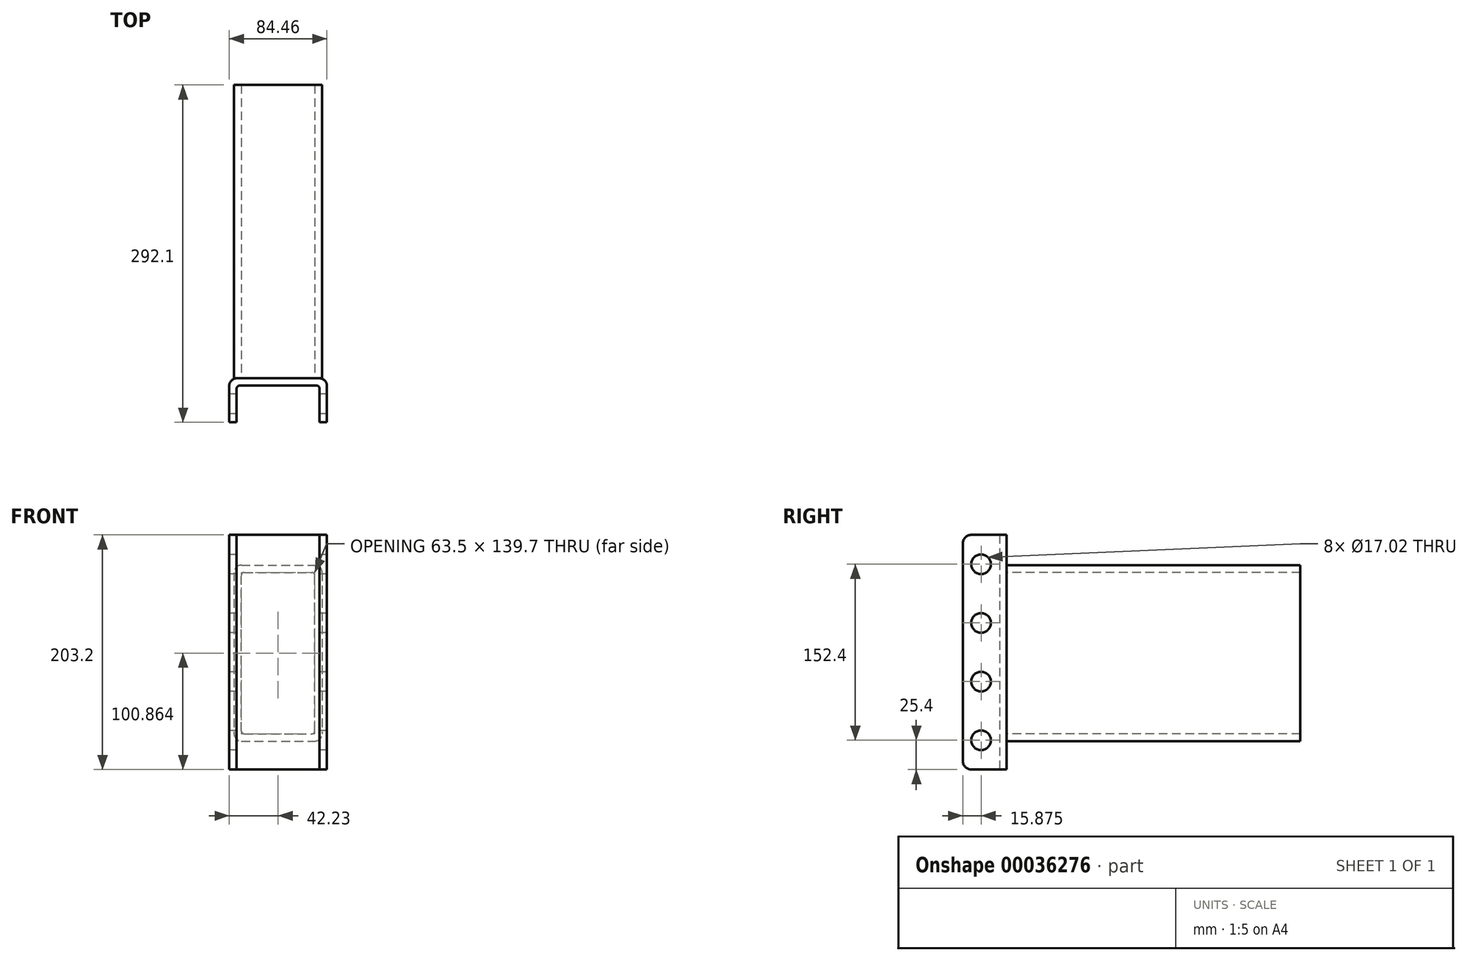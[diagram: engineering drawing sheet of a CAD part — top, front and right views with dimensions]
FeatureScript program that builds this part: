
annotation { "Feature Type Name" : "Feature", "Feature Type Description" : "" }
export const myFeature = defineFeature(function(context is Context, id is Id, definition is map)
    precondition{}
    {
        {
            var Q0;
            Q0=qCreatedBy(makeId("Top.planeOp"),FACE);
            var sketch = newSketch(context, id + "F0", { "sketchPlane" : qUnion([Q0])});
            skLineSegment(sketch, "E0", {"start": v(0, 0) * mm, "end": v(-35.88, 0) * mm});
            skLineSegment(sketch, "E1", {"start": v(-35.88, 0) * mm, "end": v(-35.88, -31.75) * mm});
            skLineSegment(sketch, "E2", {"start": v(0, 0) * mm, "end": v(0, -17.06) * mm, "construction": true});
            skLineSegment(sketch, "E3.MirrorCS", {"start": v(0, 0) * mm, "end": v(35.88, 0) * mm});
            skLineSegment(sketch, "E4.MirrorCS", {"start": v(35.88, 0) * mm, "end": v(35.88, -31.75) * mm});
            skLineSegment(sketch, "E5", {"start": v(-35.88, -31.75) * mm, "end": v(-42.23, -31.75) * mm});
            skLineSegment(sketch, "E6", {"start": v(-42.23, -31.75) * mm, "end": v(-42.23, 6.35) * mm});
            skLineSegment(sketch, "E7", {"start": v(-42.23, 6.35) * mm, "end": v(0, 6.35) * mm});
            skLineSegment(sketch, "E8.MirrorCS", {"start": v(42.23, 6.35) * mm, "end": v(0, 6.35) * mm});
            skLineSegment(sketch, "E9.MirrorCS", {"start": v(42.23, -31.75) * mm, "end": v(42.23, 6.35) * mm});
            skLineSegment(sketch, "E10.MirrorCS", {"start": v(35.88, -31.75) * mm, "end": v(42.23, -31.75) * mm});
            skLineSegment(sketch, "E11", {"start": v(0, 0) * mm, "end": v(0, 6.35) * mm, "construction": true});
            skSolve(sketch);
        }
        {
            var Q0;
            Q0=makeQuery(id+"F0.imprint","IMPRINT",FACE,{"disambiguationData":[TD([[makeQuery(id+"F0.imprint","IMPRINT",EDGE,{"derivedFrom":sQuery(id+"F0.wireOp",EDGE,"E0")}),-1.0]])]});
            extrude(context, id + "F1", {"entities" : qUnion([Q0]), "depth" : 203.2 * mm});
        }
        {
            var Q0;
            Q0=makeQuery(id+"F1.opExtrude","SWEPT_EDGE",EDGE,{"disambiguationData":[OSD([sQuery(id+"F0.wireOp",EDGE,"E8.MirrorCS"),sQuery(id+"F0.wireOp",EDGE,"E9.MirrorCS")])]});
            var Q1;
            Q1=makeQuery(id+"F1.opExtrude","SWEPT_EDGE",EDGE,{"disambiguationData":[OSD([sQuery(id+"F0.wireOp",EDGE,"E6"),sQuery(id+"F0.wireOp",EDGE,"E7")])]});
            fillet(context, id + "F2", {"entities" : qUnion([Q0, Q1]), "radius" : 6.35 * mm, "tangentPropagation" : true, "allowEdgeOverflow" : false});
        }
        {
            var Q0;
            Q0=makeQuery(id+"F1.opExtrude","CAP_EDGE",EDGE,{"disambiguationData":[OSD([sQuery(id+"F0.wireOp",EDGE,"E5")])],"isStart":false});
            var Q1;
            Q1=makeQuery(id+"F1.opExtrude","CAP_EDGE",EDGE,{"disambiguationData":[OSD([sQuery(id+"F0.wireOp",EDGE,"E10.MirrorCS")])],"isStart":false});
            var Q2;
            Q2=makeQuery(id+"F1.opExtrude","CAP_EDGE",EDGE,{"disambiguationData":[OSD([sQuery(id+"F0.wireOp",EDGE,"E5")])],"isStart":true});
            var Q3;
            Q3=makeQuery(id+"F1.opExtrude","CAP_EDGE",EDGE,{"disambiguationData":[OSD([sQuery(id+"F0.wireOp",EDGE,"E10.MirrorCS")])],"isStart":true});
            fillet(context, id + "F3", {"entities" : qUnion([Q0, Q1, Q2, Q3]), "radius" : 7.62 * mm, "tangentPropagation" : true, "allowEdgeOverflow" : false});
        }
        {
            var Q0;
            Q0=makeQuery(id+"F1.opExtrude","SWEPT_FACE",FACE,{"disambiguationData":[OSD([sQuery(id+"F0.wireOp",EDGE,"E6")])]});
            var sketch = newSketch(context, id + "F4", { "sketchPlane" : qUnion([Q0])});
            skCircle(sketch, "E12", {"center": v(15.88, 25.4) * mm, "radius": 8.5 * mm});
            skLineSegment(sketch, "E13", {"start": v(0, 101.6) * mm, "end": v(31.75, 101.6) * mm, "construction": true});
            skLineSegment(sketch, "E14", {"start": v(15.87, 203.2) * mm, "end": v(15.88, 0) * mm, "construction": true});
            skPoint(sketch, "E15", {"position": v(15.88, 101.6) * mm});
            skCircle(sketch, "E16.0.1.0", {"center": v(15.88, 76.2) * mm, "radius": 8.5 * mm});
            skCircle(sketch, "E16.0.2.0", {"center": v(15.88, 127) * mm, "radius": 8.5 * mm});
            skCircle(sketch, "E16.0.3.0", {"center": v(15.88, 177.8) * mm, "radius": 8.5 * mm});
            skLineSegment(sketch, "E16.direction1", {"start": v(15.88, 25.4) * mm, "end": v(40.64, 25.4) * mm, "construction": true});
            skLineSegment(sketch, "E16.direction2", {"start": v(15.88, 25.4) * mm, "end": v(15.88, 76.2) * mm, "construction": true});
            skLineSegment(sketch, "E17", {"start": v(15.87, 177.8) * mm, "end": v(15.87, 203.2) * mm, "construction": true});
            skLineSegment(sketch, "E18", {"start": v(15.88, 127) * mm, "end": v(15.88, 101.6) * mm, "construction": true});
            skLineSegment(sketch, "E19", {"start": v(15.88, 0) * mm, "end": v(15.88, 25.4) * mm, "construction": true});
            skSolve(sketch);
        }
        {
            var Q0;
            Q0=makeQuery(id+"F4.imprint","IMPRINT",FACE,{"disambiguationData":[TD([[makeQuery(id+"F4.imprint","IMPRINT",EDGE,{"derivedFrom":sQuery(id+"F4.wireOp",EDGE,"E16.0.3.0")}),1.0]])]});
            var Q1;
            Q1=makeQuery(id+"F4.imprint","IMPRINT",FACE,{"disambiguationData":[TD([[makeQuery(id+"F4.imprint","IMPRINT",EDGE,{"derivedFrom":sQuery(id+"F4.wireOp",EDGE,"E16.0.2.0")}),1.0]])]});
            var Q2;
            Q2=makeQuery(id+"F4.imprint","IMPRINT",FACE,{"disambiguationData":[TD([[makeQuery(id+"F4.imprint","IMPRINT",EDGE,{"derivedFrom":sQuery(id+"F4.wireOp",EDGE,"E16.0.1.0")}),1.0]])]});
            var Q3;
            Q3=makeQuery(id+"F4.imprint","IMPRINT",FACE,{"disambiguationData":[TD([[makeQuery(id+"F4.imprint","IMPRINT",EDGE,{"derivedFrom":sQuery(id+"F4.wireOp",EDGE,"E12")}),1.0]])]});
            extrude(context, id + "F5", {"entities" : qUnion([Q0, Q1, Q2, Q3]), "operationType" : NewBodyOperationType.REMOVE, "endBound" : BoundingType.THROUGH_ALL, "oppositeDirection" : true, "depth" : 25.4 * mm});
        }
        {
            var Q0;
            Q0=makeQuery(id+"F1.opExtrude","SWEPT_EDGE",EDGE,{"disambiguationData":[OSD([sQuery(id+"F0.wireOp",EDGE,"E3.MirrorCS"),sQuery(id+"F0.wireOp",EDGE,"E4.MirrorCS")])]});
            var Q1;
            Q1=makeQuery(id+"F1.opExtrude","SWEPT_EDGE",EDGE,{"disambiguationData":[OSD([sQuery(id+"F0.wireOp",EDGE,"E0"),sQuery(id+"F0.wireOp",EDGE,"E1")])]});
            fillet(context, id + "F6", {"entities" : qUnion([Q0, Q1]), "radius" : 2.54 * mm, "tangentPropagation" : true, "allowEdgeOverflow" : false});
        }
        {
            var Q0;
            Q0=makeQuery(id+"F1.opExtrude","SWEPT_FACE",FACE,{"disambiguationData":[OSD([sQuery(id+"F0.wireOp",EDGE,"E7"),sQuery(id+"F0.wireOp",EDGE,"E8.MirrorCS")])]});
            var sketch = newSketch(context, id + "F7", { "sketchPlane" : qUnion([Q0])});
            skLineSegment(sketch, "E20.rect.bottom", {"start": v(38.1, 177.06) * mm, "end": v(-38.1, 177.06) * mm});
            skLineSegment(sketch, "E20.rect.top", {"start": v(38.1, 24.66) * mm, "end": v(-38.1, 24.66) * mm});
            skLineSegment(sketch, "E20.rect.left", {"start": v(38.1, 177.06) * mm, "end": v(38.1, 24.66) * mm});
            skLineSegment(sketch, "E20.rect.right", {"start": v(-38.1, 177.06) * mm, "end": v(-38.1, 24.66) * mm});
            skPoint(sketch, "E20.rect.middle", {"position": v(0, 100.86) * mm});
            skLineSegment(sketch, "E21.rect.bottom", {"start": v(31.75, 31.01) * mm, "end": v(-31.75, 31.01) * mm});
            skLineSegment(sketch, "E21.rect.top", {"start": v(31.75, 170.71) * mm, "end": v(-31.75, 170.71) * mm});
            skLineSegment(sketch, "E21.rect.left", {"start": v(31.75, 31.01) * mm, "end": v(31.75, 170.71) * mm});
            skLineSegment(sketch, "E21.rect.right", {"start": v(-31.75, 31.01) * mm, "end": v(-31.75, 170.71) * mm});
            skSolve(sketch);
        }
        {
            var Q0;
            {var subQ6=sQuery(id+"F7.wireOp",EDGE,"E20.rect.left");Q0=makeQuery(id+"F7.imprint","IMPRINT",FACE,{"disambiguationData":[TD([[makeQuery(id+"F7.imprint","IMPRINT",EDGE,{"derivedFrom":subQ6}),-1.0]])]});}
            var Q1;
            Q1=makeQuery(id+"F7.imprint","IMPRINT",FACE,{"disambiguationData":[TD([[makeQuery(id+"F7.imprint","IMPRINT",EDGE,{"derivedFrom":sQuery(id+"F7.wireOp",EDGE,"E21.rect.bottom")}),1.0]])]});
            var Q2;
            {var subQ6=sQuery(id+"F7.wireOp",EDGE,"E20.rect.right");Q2=makeQuery(id+"F7.imprint","IMPRINT",FACE,{"disambiguationData":[TD([[makeQuery(id+"F7.imprint","IMPRINT",EDGE,{"derivedFrom":subQ6}),1.0]])]});}
            extrude(context, id + "F8", {"entities" : qUnion([Q0, Q1, Q2]), "depth" : 254 * mm});
        }
        {
            var Q0;
            Q0=makeQuery(id+"F8.opExtrude","SWEPT_EDGE",EDGE,{"disambiguationData":[OSD([sQuery(id+"F0.wireOp",EDGE,"E7"),sQuery(id+"F0.wireOp",EDGE,"E8.MirrorCS"),sQuery(id+"F0.wireOp",EDGE,"E9.MirrorCS"),sQuery(id+"F7.wireOp",EDGE,"E20.rect.bottom")])]});
            var Q1;
            Q1=makeQuery(id+"F8.opExtrude","SWEPT_EDGE",EDGE,{"disambiguationData":[OSD([sQuery(id+"F0.wireOp",EDGE,"E6"),sQuery(id+"F0.wireOp",EDGE,"E7"),sQuery(id+"F0.wireOp",EDGE,"E8.MirrorCS"),sQuery(id+"F7.wireOp",EDGE,"E20.rect.bottom")])]});
            var Q2;
            Q2=makeQuery(id+"F8.opExtrude","SWEPT_EDGE",EDGE,{"disambiguationData":[OSD([sQuery(id+"F0.wireOp",EDGE,"E7"),sQuery(id+"F0.wireOp",EDGE,"E8.MirrorCS"),sQuery(id+"F0.wireOp",EDGE,"E9.MirrorCS"),sQuery(id+"F7.wireOp",EDGE,"E20.rect.top")])]});
            var Q3;
            Q3=makeQuery(id+"F8.opExtrude","SWEPT_EDGE",EDGE,{"disambiguationData":[OSD([sQuery(id+"F0.wireOp",EDGE,"E6"),sQuery(id+"F0.wireOp",EDGE,"E7"),sQuery(id+"F0.wireOp",EDGE,"E8.MirrorCS"),sQuery(id+"F7.wireOp",EDGE,"E20.rect.top")])]});
            fillet(context, id + "F9", {"entities" : qUnion([Q0, Q1, Q2, Q3]), "radius" : 6.35 * mm, "tangentPropagation" : true, "allowEdgeOverflow" : false});
        }
        {
            var Q0;
            Q0=makeQuery(id+"F8.opExtrude","SWEPT_EDGE",EDGE,{"disambiguationData":[OSD([sQuery(id+"F7.wireOp",EDGE,"E21.rect.top"),sQuery(id+"F7.wireOp",EDGE,"E21.rect.right")])]});
            var Q1;
            Q1=makeQuery(id+"F8.opExtrude","SWEPT_EDGE",EDGE,{"disambiguationData":[OSD([sQuery(id+"F7.wireOp",EDGE,"E21.rect.top"),sQuery(id+"F7.wireOp",EDGE,"E21.rect.left")])]});
            var Q2;
            Q2=makeQuery(id+"F8.opExtrude","SWEPT_EDGE",EDGE,{"disambiguationData":[OSD([sQuery(id+"F7.wireOp",EDGE,"E21.rect.bottom"),sQuery(id+"F7.wireOp",EDGE,"E21.rect.left")])]});
            var Q3;
            Q3=makeQuery(id+"F8.opExtrude","SWEPT_EDGE",EDGE,{"disambiguationData":[OSD([sQuery(id+"F7.wireOp",EDGE,"E21.rect.bottom"),sQuery(id+"F7.wireOp",EDGE,"E21.rect.right")])]});
            fillet(context, id + "F10", {"entities" : qUnion([Q0, Q1, Q2, Q3]), "radius" : 2.54 * mm, "tangentPropagation" : true, "allowEdgeOverflow" : false});
        }
    });
